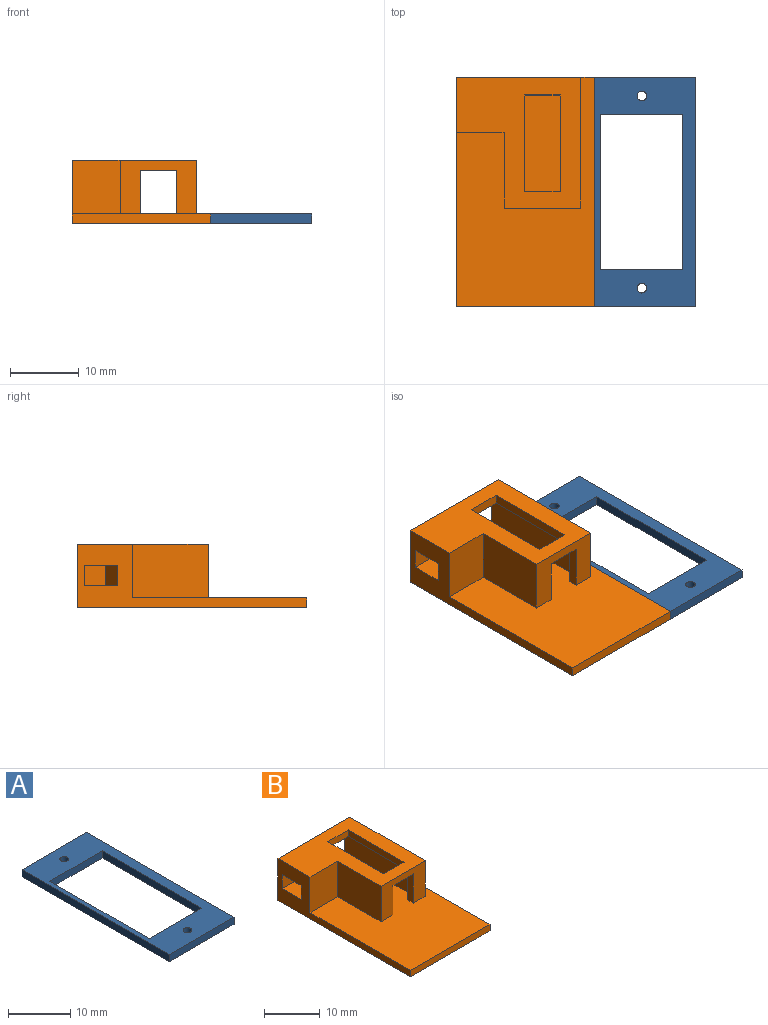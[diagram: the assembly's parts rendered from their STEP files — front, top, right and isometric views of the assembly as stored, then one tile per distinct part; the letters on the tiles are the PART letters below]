
ASSEMBLY  parts=2 mates=1
PART A: 12 faces, bbox 14.8x33.5x1.4 mm
  f0: plane 33.5x14.8mm, normal (0,0,1), area 220.8mm2, adj f1,f2,f3,f5,f6,f7,f8,f9
  f1: plane 14.8x1.4mm, normal (0,1,0), area 20.7mm2, adj f0,f2,f4,f11
  f2: plane 33.5x1.4mm, normal (-1,0,0), area 46.9mm2, adj f0,f1,f3,f4
  f3: plane 14.8x1.4mm, normal (0,-1,0), area 20.7mm2, adj f0,f2,f4,f11
  f4: plane 33.5x14.8mm, normal (0,0,-1), area 220.8mm2, adj f1,f2,f3,f5,f6,f7,f8,f9
  f5: cylinder r=0.7mm len=1.4mm, axis (0,0,-1), area 6.2mm2, adj f0,f4
  f6: cylinder r=0.7mm len=1.4mm, axis (0,0,-1), area 6.2mm2, adj f0,f4
  f7: plane 12x1.4mm, normal (0,1,0), area 16.8mm2, adj f0,f4,f9,f10
  f8: plane 12x1.4mm, normal (0,-1,0), area 16.8mm2, adj f0,f4,f9,f10
  f9: plane 22.66x1.4mm, normal (1,0,0), area 31.7mm2, adj f0,f4,f7,f8
  f10: plane 22.66x1.4mm, normal (-1,0,0), area 31.7mm2, adj f0,f4,f7,f8
  f11: plane 33.5x1.4mm, normal (1,0,0), area 46.9mm2, adj f0,f1,f3,f4
PART B: 28 faces, bbox 20.2x33.5x9.2 mm
  f0: plane 6.4x1.4mm, normal (1,0,0), area 9mm2, adj f5,f9,f12,f17
  f1: plane 14.15x1.4mm, normal (-1,0,0), area 19.8mm2, adj f16,f17,f18,f19
  f2: plane 14.15x1.4mm, normal (1,0,0), area 19.8mm2, adj f16,f17,f18,f19
  f3: plane 20.2x9.2mm, normal (0,1,0), area 116.5mm2, adj f5,f7,f8,f10,f13,f14,f16,f17
  f4: plane 6.4x1.4mm, normal (-1,0,0), area 9mm2, adj f5,f12,f15,f17
  f5: plane 33.5x20.2mm, normal (0,0,1), area 562mm2, adj f0,f3,f4,f6,f7,f9,f10,f11
  f6: plane 20.2x1.4mm, normal (0,-1,0), area 28.3mm2, adj f5,f7,f8,f27
  f7: plane 33.5x1.4mm, normal (1,0,0), area 46.9mm2, adj f3,f5,f6,f8
  f8: plane 33.5x20.2mm, normal (0,0,-1), area 676.7mm2, adj f3,f6,f7,f27
  f9: plane 6.4x1.63mm, normal (0,1,0), area 10.4mm2, adj f0,f5,f10,f17
  f10: plane 17.7x6.4mm, normal (1,0,0), area 104.3mm2, adj f3,f5,f9,f17,f20,f21,f22,f23
  f11: plane 11x7.8mm, normal (-1,0,0), area 85.8mm2, adj f5,f12,f16,f24
  f12: plane 11.2x7.8mm, normal (0,-1,0), area 54.4mm2, adj f0,f4,f5,f11,f13,f16,f17
  f13: plane 19.1x7.8mm, normal (1,0,0), area 149mm2, adj f3,f5,f12,f16
  f14: plane 17.7x6.4mm, normal (-1,0,0), area 113.3mm2, adj f3,f5,f15,f17
  f15: plane 6.4x1.63mm, normal (0,1,0), area 10.4mm2, adj f4,f5,f14,f17
  f16: plane 19.1x18.2mm, normal (0,0,1), area 197.8mm2, adj f1,f2,f3,f11,f12,f13,f18,f19
  f17: plane 19.1x8.4mm, normal (0,0,-1), area 83.1mm2, adj f0,f1,f2,f3,f4,f9,f10,f12
  f18: plane 5.15x1.4mm, normal (0,-1,0), area 7.2mm2, adj f1,f2,f16,f17
  f19: plane 5.15x1.4mm, normal (0,1,0), area 7.2mm2, adj f1,f2,f16,f17
  f20: plane 3x0.4mm, normal (0,1,0), area 1.2mm2, adj f10,f21,f23,f25
  f21: plane 8.4x4.73mm, normal (0,0,-1), area 36.5mm2, adj f10,f20,f22,f25,f26,f27
  f22: plane 8.4x3mm, normal (0,-1,0), area 25.2mm2, adj f10,f21,f23,f27
  f23: plane 8.4x4.73mm, normal (0,0,1), area 36.5mm2, adj f10,f20,f22,f25,f26,f27
  f24: plane 7.8x7mm, normal (0,-1,0), area 54.6mm2, adj f5,f11,f16,f27
  f25: plane 3x3mm, normal (-0.5,0.87,0), area 10.4mm2, adj f20,f21,f23,f26
  f26: plane 5x3mm, normal (0,1,0), area 15mm2, adj f21,f23,f25,f27
  f27: plane 33.5x9.2mm, normal (-1,0,0), area 95.9mm2, adj f3,f5,f6,f8,f16,f21,f22,f23
PLACE A at identity
PLACE B t=(0,0,-2.1)mm
MATE fastened B.f7 <-> A.f2  axis (1,0,0) through (-6.9,0,-2.8)mm
